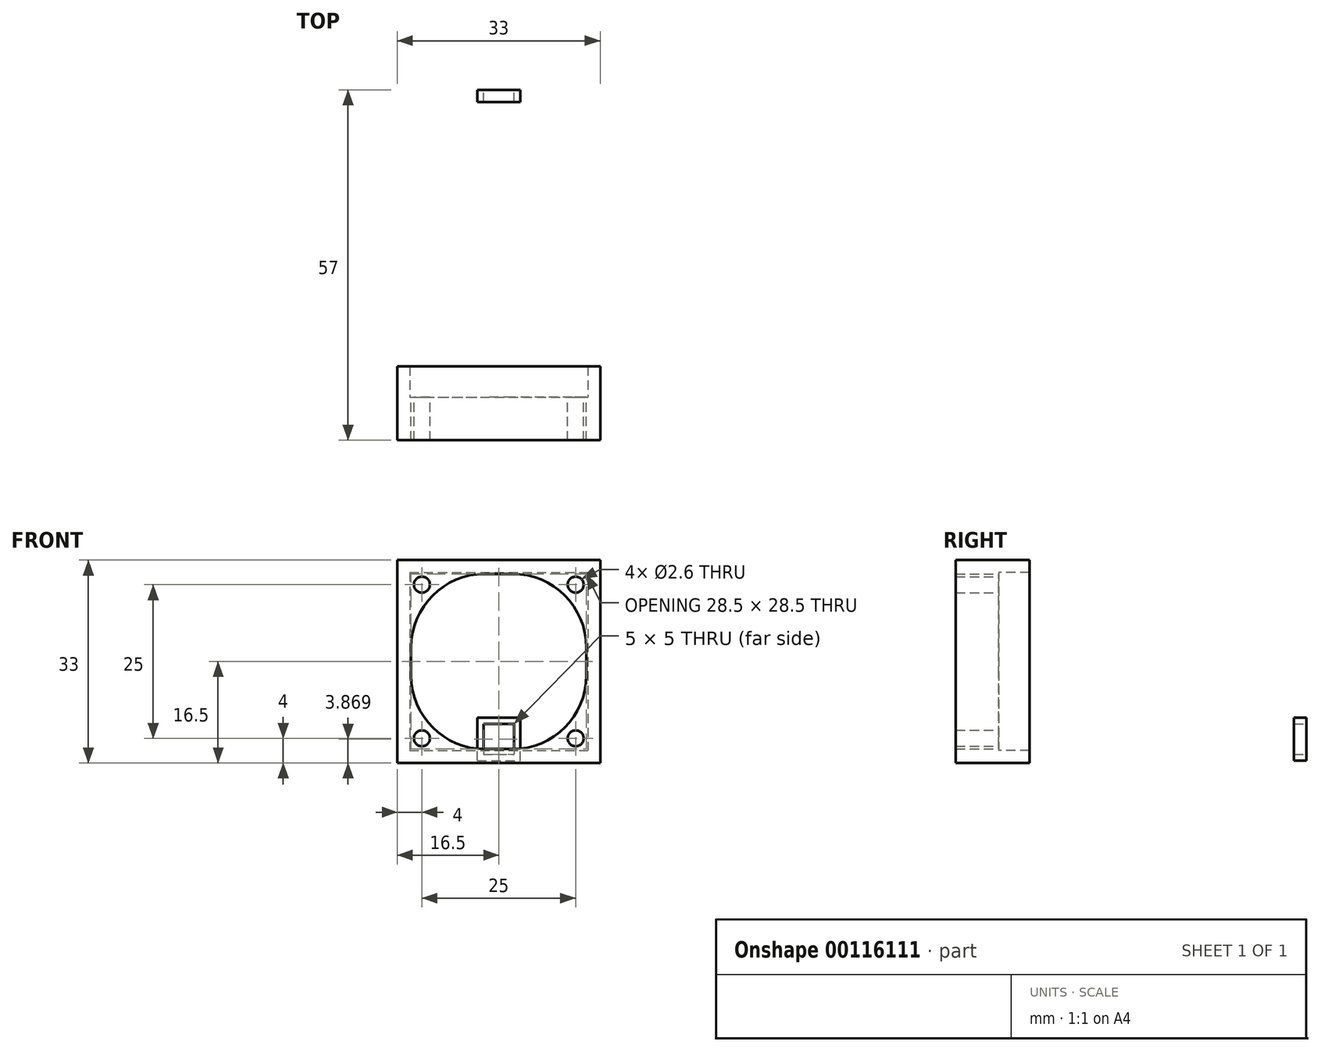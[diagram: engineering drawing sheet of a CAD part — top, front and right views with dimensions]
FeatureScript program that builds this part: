
annotation { "Feature Type Name" : "Feature", "Feature Type Description" : "" }
export const myFeature = defineFeature(function(context is Context, id is Id, definition is map)
    precondition{}
    {
        {
            var Q0;
            Q0=qCreatedBy(makeId("Front.planeOp"),FACE);
            var sketch = newSketch(context, id + "F0", { "sketchPlane" : qUnion([Q0])});
            skCircle(sketch, "E0", {"center": v(-12.5, 12.5) * mm, "radius": 1.3 * mm});
            skLineSegment(sketch, "E1.bottom", {"start": v(16.5, 16.5) * mm, "end": v(-16.5, 16.5) * mm});
            skLineSegment(sketch, "E1.top", {"start": v(16.5, -16.5) * mm, "end": v(-16.5, -16.5) * mm});
            skLineSegment(sketch, "E1.left", {"start": v(16.5, 16.5) * mm, "end": v(16.5, -16.5) * mm});
            skLineSegment(sketch, "E1.right", {"start": v(-16.5, 16.5) * mm, "end": v(-16.5, -16.5) * mm});
            skPoint(sketch, "E1.middle", {"position": v(0, 0) * mm});
            skCircle(sketch, "E2", {"center": v(12.5, 12.5) * mm, "radius": 1.3 * mm});
            skCircle(sketch, "E3", {"center": v(-12.5, -12.5) * mm, "radius": 1.3 * mm});
            skCircle(sketch, "E4", {"center": v(12.5, -12.5) * mm, "radius": 1.3 * mm});
            skLineSegment(sketch, "E5.bottom", {"start": v(2.25, -14.25) * mm, "end": v(-2.25, -14.25) * mm});
            skLineSegment(sketch, "E5.top", {"start": v(2.25, 14.25) * mm, "end": v(-2.25, 14.25) * mm});
            skLineSegment(sketch, "E5.left", {"start": v(14.25, -2.25) * mm, "end": v(14.25, 2.25) * mm});
            skLineSegment(sketch, "E5.right", {"start": v(-14.25, -2.25) * mm, "end": v(-14.25, 2.25) * mm});
            skPoint(sketch, "E6.visualSharp", {"position": v(-14.25, 14.25) * mm});
            skArc(sketch, "E6.filletArc", {"start": v(-2.25, 14.25) * mm, "mid": v(-10.74, 10.74) * mm, "end": v(-14.25, 2.25) * mm});
            skPoint(sketch, "E7.visualSharp", {"position": v(14.25, 14.25) * mm});
            skArc(sketch, "E7.filletArc", {"start": v(14.25, 2.25) * mm, "mid": v(10.74, 10.74) * mm, "end": v(2.25, 14.25) * mm});
            skPoint(sketch, "E8.visualSharp", {"position": v(14.25, -14.25) * mm});
            skArc(sketch, "E8.filletArc", {"start": v(2.25, -14.25) * mm, "mid": v(10.74, -10.74) * mm, "end": v(14.25, -2.25) * mm});
            skPoint(sketch, "E9.visualSharp", {"position": v(-14.25, -14.25) * mm});
            skArc(sketch, "E9.filletArc", {"start": v(-14.25, -2.25) * mm, "mid": v(-10.74, -10.74) * mm, "end": v(-2.25, -14.25) * mm});
            skSolve(sketch);
        }
        {
            var Q0;
            Q0=qCreatedBy(makeId("Front.planeOp"),FACE);
            cPlane(context, id + "F1", {"entities" : qUnion([Q0]), "cplaneType" : CPlaneType.OFFSET, "offset" : 50 * mm, "oppositeDirection" : true, "width" : 150 * mm, "height" : 150 * mm});
        }
        {
            var Q0;
            Q0=makeQuery(id+"F0.imprint","IMPRINT",FACE,{"disambiguationData":[TD([[makeQuery(id+"F0.imprint","IMPRINT",EDGE,{"derivedFrom":sQuery(id+"F0.wireOp",EDGE,"E0")}),-1.0]])]});
            extrude(context, id + "F2", {"entities" : qUnion([Q0]), "depth" : 7 * mm});
        }
        {
            var Q0;
            Q0=makeQuery(id+"F2.opExtrude","CAP_FACE",FACE,{"disambiguationData":[OSD([sQuery(id+"F0.wireOp",EDGE,"E0"),sQuery(id+"F0.wireOp",EDGE,"E1.bottom"),sQuery(id+"F0.wireOp",EDGE,"E1.top"),sQuery(id+"F0.wireOp",EDGE,"E1.left"),sQuery(id+"F0.wireOp",EDGE,"E1.right"),sQuery(id+"F0.wireOp",EDGE,"E2"),sQuery(id+"F0.wireOp",EDGE,"E3"),sQuery(id+"F0.wireOp",EDGE,"E4"),sQuery(id+"F0.wireOp",EDGE,"E5.bottom"),sQuery(id+"F0.wireOp",EDGE,"E5.top"),sQuery(id+"F0.wireOp",EDGE,"E5.left"),sQuery(id+"F0.wireOp",EDGE,"E5.right"),sQuery(id+"F0.wireOp",EDGE,"E6.filletArc"),sQuery(id+"F0.wireOp",EDGE,"E7.filletArc"),sQuery(id+"F0.wireOp",EDGE,"E8.filletArc"),sQuery(id+"F0.wireOp",EDGE,"E9.filletArc")])],"isStart":true});
            var sketch = newSketch(context, id + "F3", { "sketchPlane" : qUnion([Q0])});
            skLineSegment(sketch, "E10.bottom", {"start": v(16.5, 16.5) * mm, "end": v(-16.5, 16.5) * mm});
            skLineSegment(sketch, "E10.top", {"start": v(16.5, -16.5) * mm, "end": v(-16.5, -16.5) * mm});
            skLineSegment(sketch, "E10.left", {"start": v(16.5, 16.5) * mm, "end": v(16.5, -16.5) * mm});
            skLineSegment(sketch, "E10.right", {"start": v(-16.5, 16.5) * mm, "end": v(-16.5, -16.5) * mm});
            skPoint(sketch, "E10.middle", {"position": v(0, 0) * mm});
            skLineSegment(sketch, "E11.bottom", {"start": v(14.5, 14.5) * mm, "end": v(-14.5, 14.5) * mm});
            skLineSegment(sketch, "E11.top", {"start": v(14.5, -14.5) * mm, "end": v(-14.5, -14.5) * mm});
            skLineSegment(sketch, "E11.left", {"start": v(14.5, 14.5) * mm, "end": v(14.5, -14.5) * mm});
            skLineSegment(sketch, "E11.right", {"start": v(-14.5, 14.5) * mm, "end": v(-14.5, -14.5) * mm});
            skSolve(sketch);
        }
        {
            var Q0;
            Q0 = qSketchRegion(id + "F3", true);
            extrude(context, id + "F4", {"entities" : qUnion([Q0]), "operationType" : NewBodyOperationType.ADD, "depth" : 5 * mm});
        }
        {
            var Q0;
            Q0=qCreatedBy(id+"F1.planeOp",FACE);
            var sketch = newSketch(context, id + "F5", { "sketchPlane" : qUnion([Q0])});
            skLineSegment(sketch, "E12.bottom", {"start": v(-3.5, -16.13) * mm, "end": v(3.5, -16.13) * mm});
            skLineSegment(sketch, "E12.top", {"start": v(-3.5, -9.13) * mm, "end": v(3.5, -9.13) * mm});
            skLineSegment(sketch, "E12.left", {"start": v(-3.5, -16.13) * mm, "end": v(-3.5, -9.13) * mm});
            skLineSegment(sketch, "E12.right", {"start": v(3.5, -16.13) * mm, "end": v(3.5, -9.13) * mm});
            skPoint(sketch, "E12.middle", {"position": v(0, -12.63) * mm});
            skLineSegment(sketch, "E13.bottom", {"start": v(-2.5, -10.13) * mm, "end": v(2.5, -10.13) * mm});
            skLineSegment(sketch, "E13.top", {"start": v(-2.5, -15.13) * mm, "end": v(2.5, -15.13) * mm});
            skLineSegment(sketch, "E13.left", {"start": v(-2.5, -10.13) * mm, "end": v(-2.5, -15.13) * mm});
            skLineSegment(sketch, "E13.right", {"start": v(2.5, -10.13) * mm, "end": v(2.5, -15.13) * mm});
            skSolve(sketch);
        }
        {
            var Q0;
            Q0=makeQuery(id+"F5.imprint","IMPRINT",FACE,{"disambiguationData":[TD([[makeQuery(id+"F5.imprint","IMPRINT",EDGE,{"derivedFrom":sQuery(id+"F5.wireOp",EDGE,"E12.bottom")}),1.0]])]});
            extrude(context, id + "F6", {"entities" : qUnion([Q0]), "depth" : 2 * mm});
        }
    });
